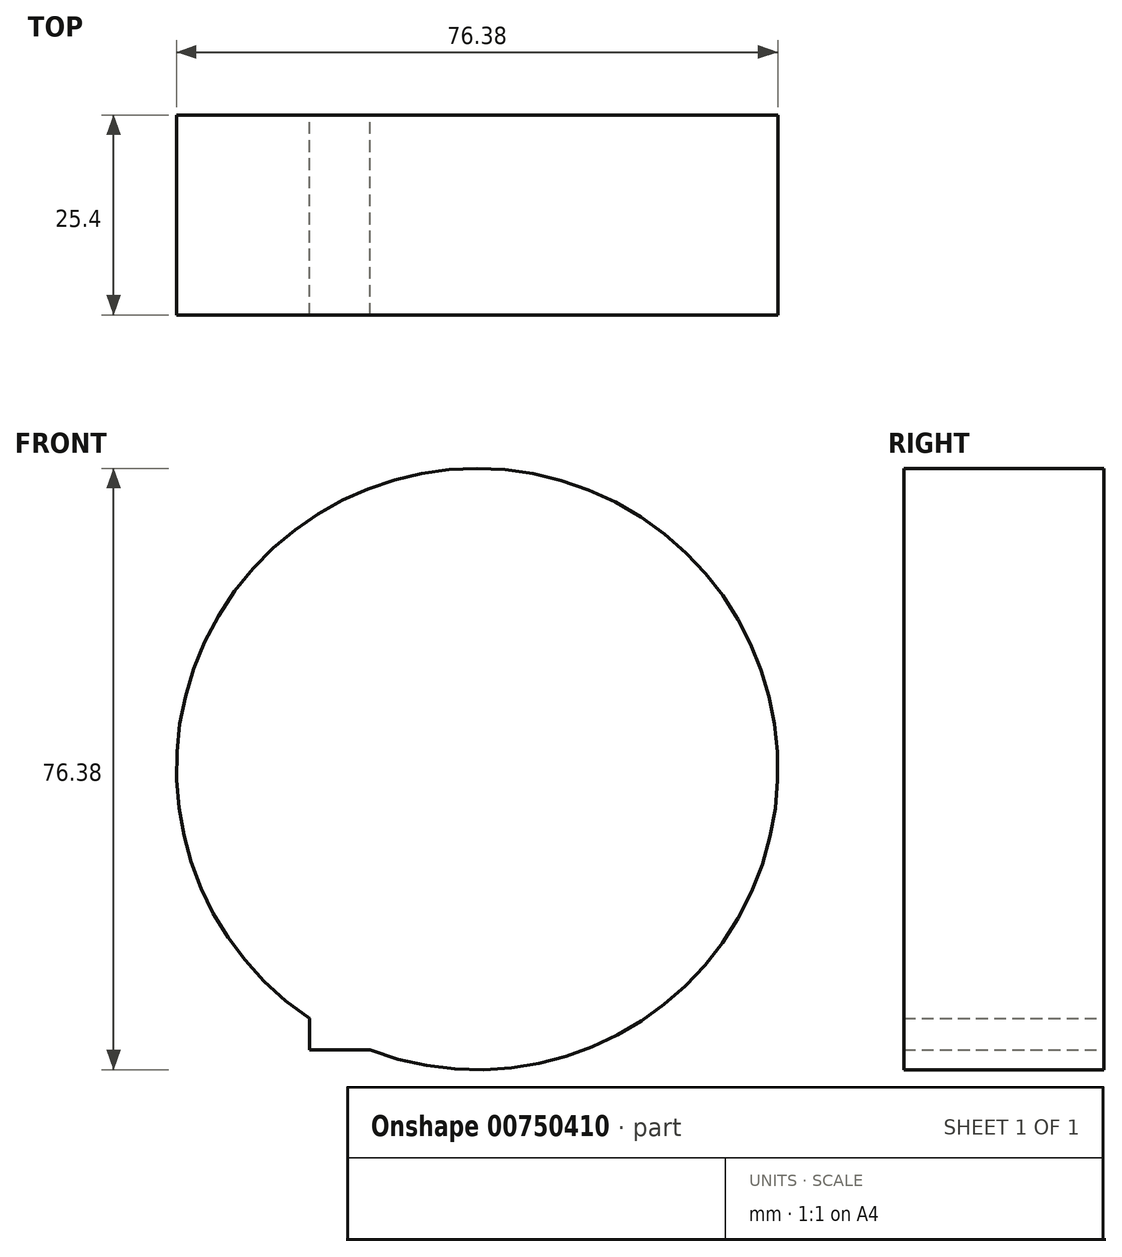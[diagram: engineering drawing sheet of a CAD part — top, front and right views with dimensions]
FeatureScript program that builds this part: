
annotation { "Feature Type Name" : "Feature", "Feature Type Description" : "" }
export const myFeature = defineFeature(function(context is Context, id is Id, definition is map)
    precondition{}
    {
        {
            var Q0;
            Q0=qCreatedBy(makeId("Front.planeOp"),FACE);
            var sketch = newSketch(context, id + "F0", { "sketchPlane" : qUnion([Q0])});
            skLineSegment(sketch, "E0.bottom", {"start": v(-21.3, 9.96) * mm, "end": v(8.9, 9.96) * mm});
            skLineSegment(sketch, "E0.top", {"start": v(-21.3, -35.69) * mm, "end": v(8.9, -35.69) * mm});
            skLineSegment(sketch, "E0.left", {"start": v(-21.3, 9.96) * mm, "end": v(-21.3, -35.69) * mm});
            skLineSegment(sketch, "E0.right", {"start": v(8.9, 9.96) * mm, "end": v(8.9, -35.69) * mm});
            skCircle(sketch, "E1", {"center": v(0, 0) * mm, "radius": 38.2 * mm});
            skSolve(sketch);
        }
        {
            var Q0;
            Q0 = qSketchRegion(id + "F0", true);
            extrude(context, id + "F1", {"entities" : qUnion([Q0]), "depth" : 25.4 * mm, "offsetDistance" : 25.4 * mm});
        }
    });
